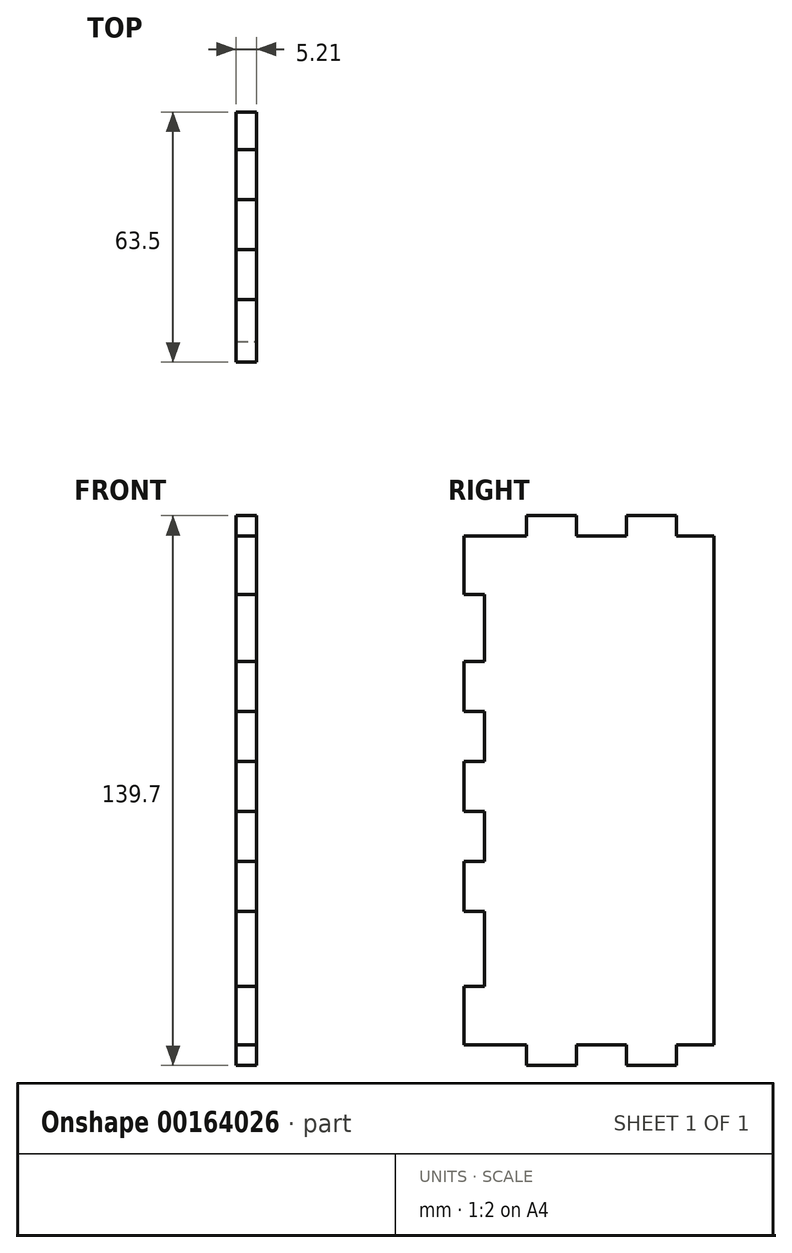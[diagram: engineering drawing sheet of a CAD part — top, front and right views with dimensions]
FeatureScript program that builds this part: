
annotation { "Feature Type Name" : "Feature", "Feature Type Description" : "" }
export const myFeature = defineFeature(function(context is Context, id is Id, definition is map)
    precondition{}
    {
        {
            var Q0;
            Q0=qCreatedBy(makeId("Right.planeOp"),FACE);
            var sketch = newSketch(context, id + "F0", { "sketchPlane" : qUnion([Q0])});
            skLineSegment(sketch, "E0.bottom", {"start": v(31.75, -69.85) * mm, "end": v(-31.75, -69.85) * mm});
            skLineSegment(sketch, "E0.top", {"start": v(31.75, 69.85) * mm, "end": v(-31.75, 69.85) * mm});
            skLineSegment(sketch, "E0.left", {"start": v(31.75, -69.85) * mm, "end": v(31.75, 69.85) * mm});
            skLineSegment(sketch, "E0.right", {"start": v(-31.75, -69.85) * mm, "end": v(-31.75, 69.85) * mm});
            skPoint(sketch, "E0.middle", {"position": v(0, 0) * mm});
            skSolve(sketch);
        }
        {
            var Q0;
            Q0=makeQuery(id+"F0.imprint","IMPRINT",FACE,{"disambiguationData":[TD([[makeQuery(id+"F0.imprint","IMPRINT",EDGE,{"derivedFrom":sQuery(id+"F0.wireOp",EDGE,"E0.bottom")}),-1.0]])]});
            extrude(context, id + "F1", {"entities" : qUnion([Q0]), "depth" : 5.2 * mm});
        }
        {
            var Q0;
            Q0=makeQuery(id+"F1.opExtrude","CAP_FACE",FACE,{"disambiguationData":[OSD([sQuery(id+"F0.wireOp",EDGE,"E0.bottom"),sQuery(id+"F0.wireOp",EDGE,"E0.top"),sQuery(id+"F0.wireOp",EDGE,"E0.left"),sQuery(id+"F0.wireOp",EDGE,"E0.right")])],"isStart":false});
            var sketch = newSketch(context, id + "F2", { "sketchPlane" : qUnion([Q0])});
            skLineSegment(sketch, "E1", {"start": v(-31.75, -64.64) * mm, "end": v(-31.75, -49.71) * mm});
            skLineSegment(sketch, "E2", {"start": v(-31.75, -49.71) * mm, "end": v(-26.54, -49.71) * mm});
            skLineSegment(sketch, "E3", {"start": v(-26.54, -49.71) * mm, "end": v(-26.54, -30.66) * mm});
            skLineSegment(sketch, "E4", {"start": v(-26.54, -30.66) * mm, "end": v(-31.75, -30.66) * mm});
            skLineSegment(sketch, "E5", {"start": v(-31.75, -30.66) * mm, "end": v(-31.75, -17.96) * mm});
            skLineSegment(sketch, "E6", {"start": v(-31.75, -17.96) * mm, "end": v(-26.54, -17.96) * mm});
            skLineSegment(sketch, "E7", {"start": v(-26.54, -17.96) * mm, "end": v(-26.54, -5.26) * mm});
            skLineSegment(sketch, "E8", {"start": v(-26.54, -5.26) * mm, "end": v(-31.75, -5.26) * mm});
            skLineSegment(sketch, "E9", {"start": v(-31.75, -5.26) * mm, "end": v(-31.75, 7.44) * mm});
            skLineSegment(sketch, "E10", {"start": v(-31.75, 7.44) * mm, "end": v(-26.54, 7.44) * mm});
            skLineSegment(sketch, "E11", {"start": v(-26.54, 7.44) * mm, "end": v(-26.54, 20.14) * mm});
            skLineSegment(sketch, "E12", {"start": v(-26.54, 20.14) * mm, "end": v(-31.75, 20.14) * mm});
            skLineSegment(sketch, "E13", {"start": v(-31.75, 20.14) * mm, "end": v(-31.75, 32.84) * mm});
            skLineSegment(sketch, "E14", {"start": v(-31.75, 32.84) * mm, "end": v(-26.54, 32.84) * mm});
            skLineSegment(sketch, "E15", {"start": v(-26.54, 32.84) * mm, "end": v(-26.54, 49.77) * mm});
            skLineSegment(sketch, "E16", {"start": v(-26.54, 49.77) * mm, "end": v(-31.75, 49.77) * mm});
            skLineSegment(sketch, "E17", {"start": v(-31.75, 49.77) * mm, "end": v(-31.75, 64.64) * mm});
            skLineSegment(sketch, "E18", {"start": v(-31.75, -64.64) * mm, "end": v(-15.87, -64.64) * mm});
            skLineSegment(sketch, "E19", {"start": v(-15.87, -64.64) * mm, "end": v(-15.87, -69.85) * mm});
            skLineSegment(sketch, "E20", {"start": v(-15.87, -69.85) * mm, "end": v(-3.17, -69.85) * mm});
            skLineSegment(sketch, "E21", {"start": v(-3.17, -69.85) * mm, "end": v(-3.17, -64.64) * mm});
            skLineSegment(sketch, "E22", {"start": v(-3.17, -64.64) * mm, "end": v(9.53, -64.64) * mm});
            skLineSegment(sketch, "E23", {"start": v(9.53, -64.64) * mm, "end": v(9.53, -69.85) * mm});
            skLineSegment(sketch, "E24", {"start": v(9.53, -69.85) * mm, "end": v(22.23, -69.85) * mm});
            skLineSegment(sketch, "E25", {"start": v(22.23, -69.85) * mm, "end": v(22.23, -64.64) * mm});
            skLineSegment(sketch, "E26", {"start": v(22.23, -64.64) * mm, "end": v(31.75, -64.64) * mm});
            skLineSegment(sketch, "E27", {"start": v(-31.75, 64.64) * mm, "end": v(-15.88, 64.64) * mm});
            skLineSegment(sketch, "E28", {"start": v(-15.88, 64.64) * mm, "end": v(-15.88, 69.85) * mm});
            skLineSegment(sketch, "E29", {"start": v(-15.88, 69.85) * mm, "end": v(-3.18, 69.85) * mm});
            skLineSegment(sketch, "E30", {"start": v(-3.18, 69.85) * mm, "end": v(-3.18, 64.64) * mm});
            skLineSegment(sketch, "E31", {"start": v(-3.18, 64.64) * mm, "end": v(9.53, 64.64) * mm});
            skLineSegment(sketch, "E32", {"start": v(9.53, 64.64) * mm, "end": v(9.53, 69.85) * mm});
            skLineSegment(sketch, "E33", {"start": v(9.53, 69.85) * mm, "end": v(22.23, 69.85) * mm});
            skLineSegment(sketch, "E34", {"start": v(22.23, 69.85) * mm, "end": v(22.23, 64.64) * mm});
            skLineSegment(sketch, "E35", {"start": v(22.23, 64.64) * mm, "end": v(31.75, 64.64) * mm});
            skSolve(sketch);
        }
        {
            var Q0;
            Q0=makeQuery(id+"F2.imprint","IMPRINT",FACE,{"disambiguationData":[TD([[makeQuery(id+"F2.imprint","IMPRINT",EDGE,{"derivedFrom":sQuery(id+"F2.wireOp",EDGE,"141f7278-a81d-4f80-8147-5e9a29097b77")}),-1.0]])]});
            var Q1;
            {var subQ0=sQuery(id+"F2.wireOp",EDGE,"E14");Q1=makeQuery(id+"F2.imprint","IMPRINT",FACE,{"disambiguationData":[TD([[makeQuery(id+"F2.imprint","IMPRINT",EDGE,{"derivedFrom":subQ0}),1.0]])]});}
            var Q2;
            {var subQ0=sQuery(id+"F2.wireOp",EDGE,"E10");Q2=makeQuery(id+"F2.imprint","IMPRINT",FACE,{"disambiguationData":[TD([[makeQuery(id+"F2.imprint","IMPRINT",EDGE,{"derivedFrom":subQ0}),1.0]])]});}
            var Q3;
            {var subQ0=sQuery(id+"F2.wireOp",EDGE,"E6");Q3=makeQuery(id+"F2.imprint","IMPRINT",FACE,{"disambiguationData":[TD([[makeQuery(id+"F2.imprint","IMPRINT",EDGE,{"derivedFrom":subQ0}),1.0]])]});}
            var Q4;
            {var subQ0=sQuery(id+"F2.wireOp",EDGE,"E2");Q4=makeQuery(id+"F2.imprint","IMPRINT",FACE,{"disambiguationData":[TD([[makeQuery(id+"F2.imprint","IMPRINT",EDGE,{"derivedFrom":subQ0}),1.0]])]});}
            var Q5;
            {var subQ0=sQuery(id+"F2.wireOp",EDGE,"E18");Q5=makeQuery(id+"F2.imprint","IMPRINT",FACE,{"disambiguationData":[TD([[makeQuery(id+"F2.imprint","IMPRINT",EDGE,{"derivedFrom":subQ0}),-1.0]])]});}
            var Q6;
            {var subQ0=sQuery(id+"F2.wireOp",EDGE,"E21");Q6=makeQuery(id+"F2.imprint","IMPRINT",FACE,{"disambiguationData":[TD([[makeQuery(id+"F2.imprint","IMPRINT",EDGE,{"derivedFrom":subQ0}),-1.0]])]});}
            var Q7;
            {var subQ0=sQuery(id+"F2.wireOp",EDGE,"E25");Q7=makeQuery(id+"F2.imprint","IMPRINT",FACE,{"disambiguationData":[TD([[makeQuery(id+"F2.imprint","IMPRINT",EDGE,{"derivedFrom":subQ0}),-1.0]])]});}
            var Q8;
            {var subQ0=sQuery(id+"F2.wireOp",EDGE,"LWx1fKOB-s3DY-jHKI-FIaq-BvCsdDDRcwNy");Q8=makeQuery(id+"F2.imprint","IMPRINT",FACE,{"disambiguationData":[TD([[makeQuery(id+"F2.imprint","IMPRINT",EDGE,{"derivedFrom":subQ0}),1.0]])]});}
            var Q9;
            {var subQ0=sQuery(id+"F2.wireOp",EDGE,"VgdS4eAK-5c6L-Srbe-R1GG-81lr2idgqL1n");Q9=makeQuery(id+"F2.imprint","IMPRINT",FACE,{"disambiguationData":[TD([[makeQuery(id+"F2.imprint","IMPRINT",EDGE,{"derivedFrom":subQ0}),1.0]])]});}
            var Q10;
            {var subQ0=sQuery(id+"F2.wireOp",EDGE,"jBDqo16x-BMif-fxQN-AUOo-bCjWh2ewSLte");Q10=makeQuery(id+"F2.imprint","IMPRINT",FACE,{"disambiguationData":[TD([[makeQuery(id+"F2.imprint","IMPRINT",EDGE,{"derivedFrom":subQ0}),1.0]])]});}
            var Q11;
            {var subQ0=sQuery(id+"F2.wireOp",EDGE,"GPIbWRm3-p2A8-0tB0-rJ1E-l1NBkJdWLd7m");Q11=makeQuery(id+"F2.imprint","IMPRINT",FACE,{"disambiguationData":[TD([[makeQuery(id+"F2.imprint","IMPRINT",EDGE,{"derivedFrom":subQ0}),1.0]])]});}
            var Q12;
            {var subQ0=sQuery(id+"F2.wireOp",EDGE,"E34");Q12=makeQuery(id+"F2.imprint","IMPRINT",FACE,{"disambiguationData":[TD([[makeQuery(id+"F2.imprint","IMPRINT",EDGE,{"derivedFrom":subQ0}),1.0]])]});}
            var Q13;
            {var subQ0=sQuery(id+"F2.wireOp",EDGE,"E30");Q13=makeQuery(id+"F2.imprint","IMPRINT",FACE,{"disambiguationData":[TD([[makeQuery(id+"F2.imprint","IMPRINT",EDGE,{"derivedFrom":subQ0}),1.0]])]});}
            var Q14;
            {var subQ0=sQuery(id+"F2.wireOp",EDGE,"E27");Q14=makeQuery(id+"F2.imprint","IMPRINT",FACE,{"disambiguationData":[TD([[makeQuery(id+"F2.imprint","IMPRINT",EDGE,{"derivedFrom":subQ0}),1.0]])]});}
            extrude(context, id + "F3", {"entities" : qUnion([Q0, Q1, Q2, Q3, Q4, Q5, Q6, Q7, Q8, Q9, Q10, Q11, Q12, Q13, Q14]), "operationType" : NewBodyOperationType.REMOVE, "endBound" : BoundingType.THROUGH_ALL, "oppositeDirection" : true, "depth" : 25.4 * mm});
        }
    });
